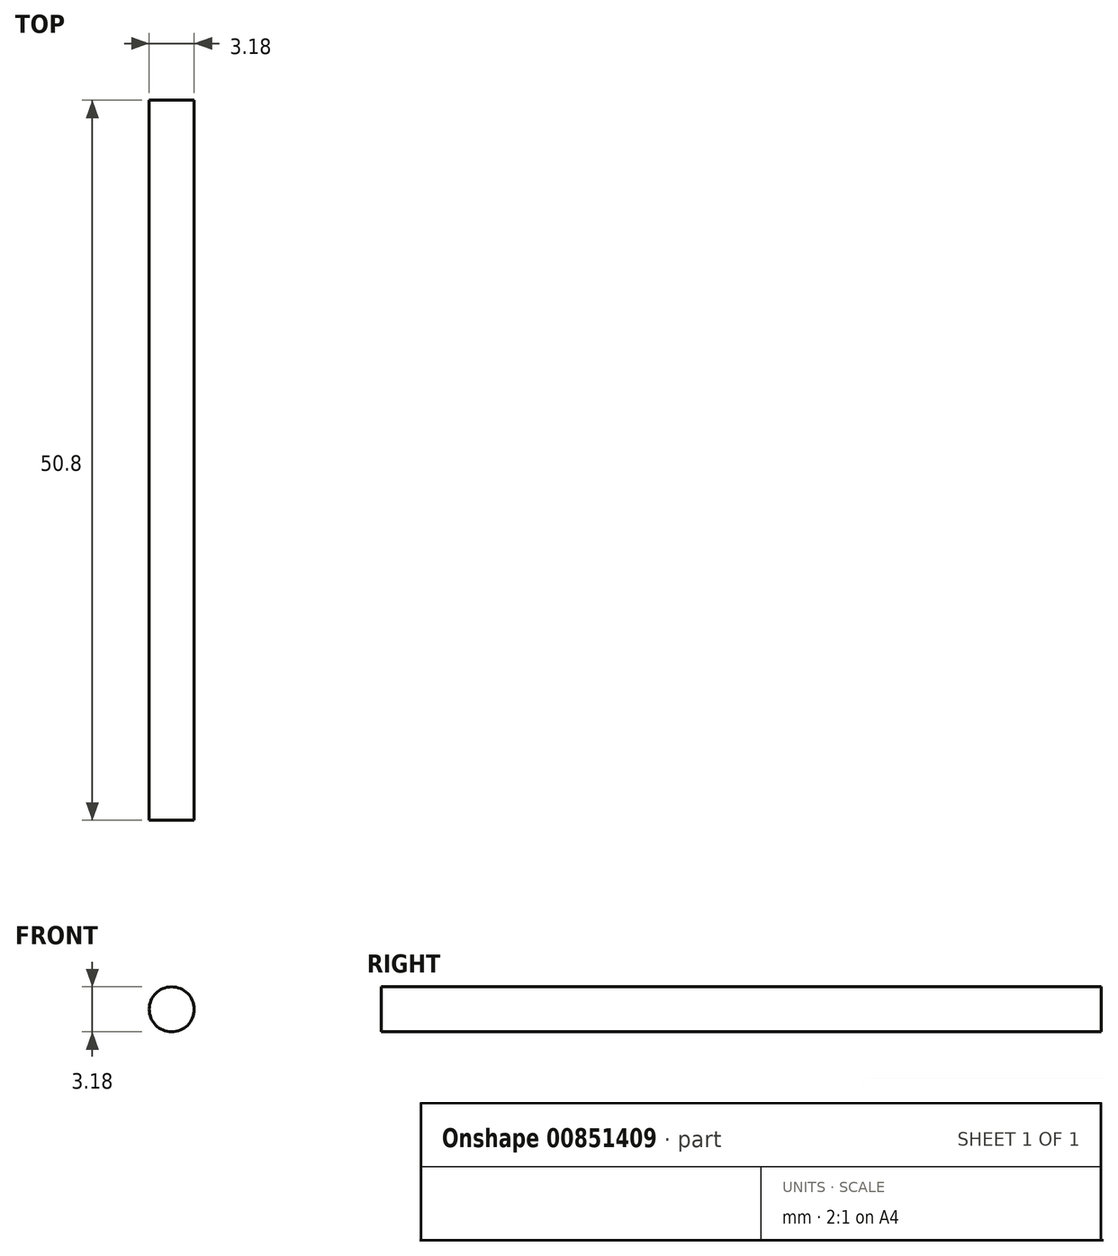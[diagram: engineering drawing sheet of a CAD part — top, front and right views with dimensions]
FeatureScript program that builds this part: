
annotation { "Feature Type Name" : "Feature", "Feature Type Description" : "" }
export const myFeature = defineFeature(function(context is Context, id is Id, definition is map)
    precondition{}
    {
        {
            var Q0;
            Q0=qCreatedBy(makeId("Front.planeOp"),FACE);
            var sketch = newSketch(context, id + "F0", { "sketchPlane" : qUnion([Q0])});
            skCircle(sketch, "E0", {"center": v(0, 0) * mm, "radius": 1.59 * mm});
            skSolve(sketch);
        }
        {
            var Q0;
            Q0 = qSketchRegion(id + "F0", true);
            extrude(context, id + "F1", {"entities" : qUnion([Q0]), "oppositeDirection" : true, "depth" : 50.8 * mm, "offsetDistance" : 25.4 * mm});
        }
    });
